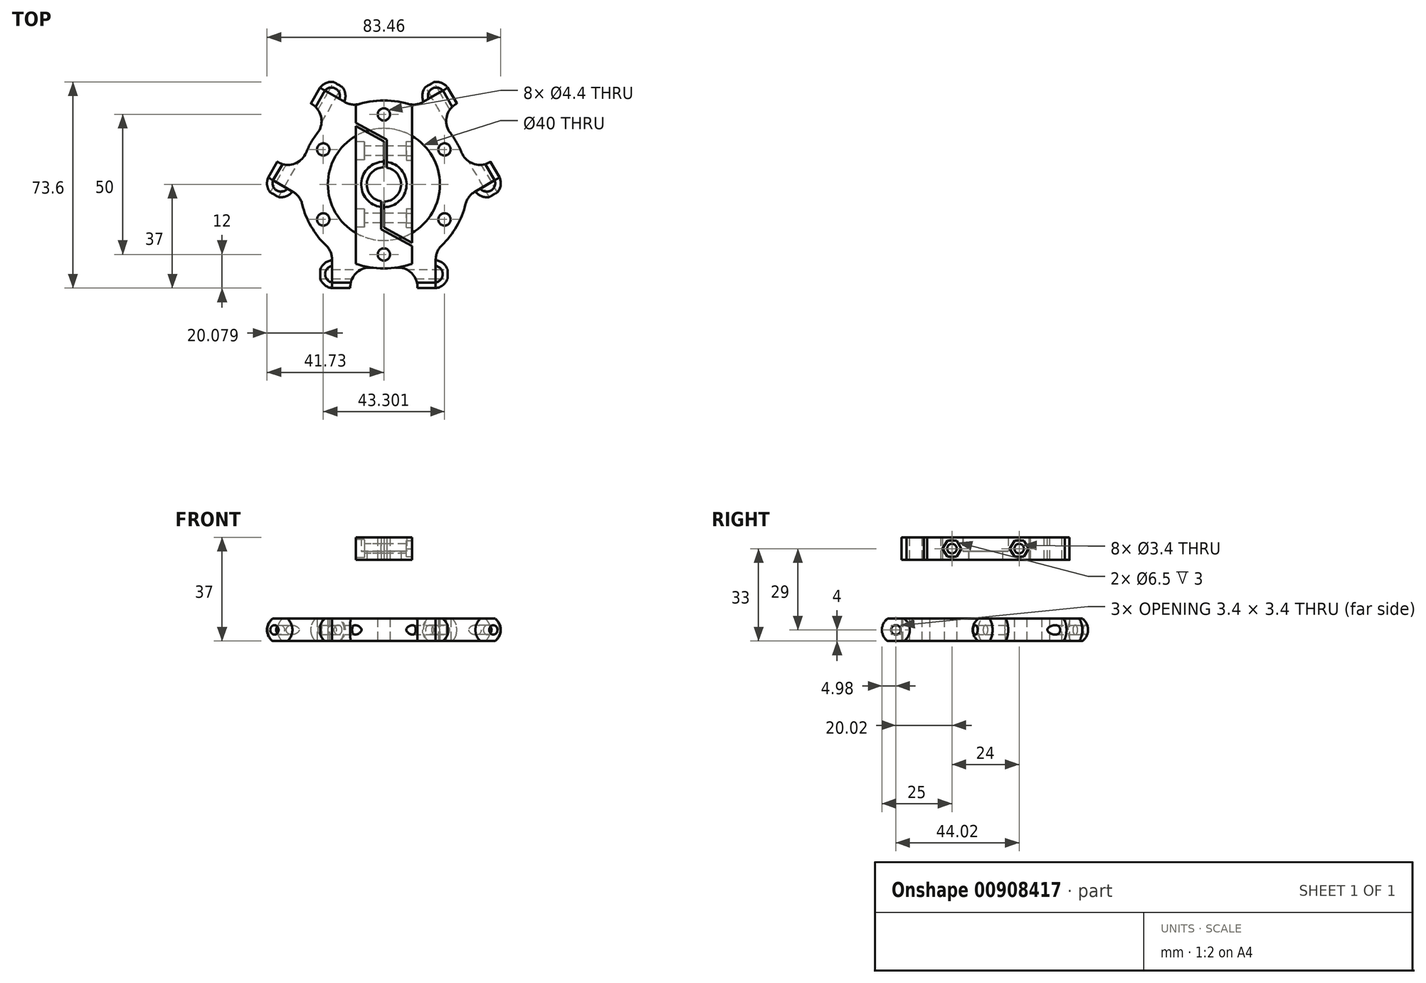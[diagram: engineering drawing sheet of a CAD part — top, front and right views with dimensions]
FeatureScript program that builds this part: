
annotation { "Feature Type Name" : "Feature", "Feature Type Description" : "" }
export const myFeature = defineFeature(function(context is Context, id is Id, definition is map)
    precondition{}
    {
        {
            var Q0;
            Q0=qCreatedBy(makeId("Top.planeOp"),FACE);
            var sketch = newSketch(context, id + "F0", { "sketchPlane" : qUnion([Q0])});
            skLineSegment(sketch, "E0", {"start": v(-16.34, 35.93) * mm, "end": v(-39.06, -3.47) * mm, "construction": true});
            skLineSegment(sketch, "E1", {"start": v(-40.4, -2.74) * mm, "end": v(-37.72, -4.2) * mm, "construction": true});
            skLineSegment(sketch, "E2", {"start": v(-17.63, 36.7) * mm, "end": v(-15.06, 35.15) * mm, "construction": true});
            skCircle(sketch, "E3", {"center": v(0, 0) * mm, "radius": 30 * mm});
            skCircle(sketch, "E4", {"center": v(0, 0) * mm, "radius": 20 * mm});
            skLineSegment(sketch, "E5", {"start": v(0, 0) * mm, "end": v(0, -43.55) * mm, "construction": true});
            skLineSegment(sketch, "E6", {"start": v(-25.45, -32) * mm, "end": v(35.74, -32) * mm, "construction": true});
            skLineSegment(sketch, "E7", {"start": v(-12, -37) * mm, "end": v(-12, -27.5) * mm});
            skLineSegment(sketch, "E8", {"start": v(-12, -37) * mm, "end": v(-18.5, -37) * mm});
            skLineSegment(sketch, "E9", {"start": v(-18.5, -37) * mm, "end": v(-18.5, -23.62) * mm});
            skLineSegment(sketch, "E10.MirrorCS", {"start": v(18.5, -37) * mm, "end": v(18.5, -23.62) * mm});
            skLineSegment(sketch, "E11.MirrorCS", {"start": v(12, -37) * mm, "end": v(12, -27.5) * mm});
            skLineSegment(sketch, "E12.MirrorCS", {"start": v(12, -37) * mm, "end": v(18.5, -37) * mm});
            skLineSegment(sketch, "E13.1.0", {"start": v(41.29, 2.48) * mm, "end": v(29.7, -4.21) * mm});
            skLineSegment(sketch, "E13.1.1", {"start": v(38.04, 8.1) * mm, "end": v(41.29, 2.48) * mm});
            skLineSegment(sketch, "E13.1.2", {"start": v(38.04, 8.1) * mm, "end": v(29.81, 3.36) * mm});
            skLineSegment(sketch, "E13.1.3", {"start": v(26.04, 28.9) * mm, "end": v(17.81, 24.14) * mm});
            skLineSegment(sketch, "E13.1.4", {"start": v(26.04, 28.9) * mm, "end": v(22.79, 34.52) * mm});
            skLineSegment(sketch, "E13.1.5", {"start": v(22.79, 34.52) * mm, "end": v(11.2, 27.83) * mm});
            skLineSegment(sketch, "E13.2.0", {"start": v(-22.79, 34.52) * mm, "end": v(-11.2, 27.83) * mm});
            skLineSegment(sketch, "E13.2.1", {"start": v(-26.04, 28.9) * mm, "end": v(-22.79, 34.52) * mm});
            skLineSegment(sketch, "E13.2.2", {"start": v(-26.04, 28.9) * mm, "end": v(-17.81, 24.14) * mm});
            skLineSegment(sketch, "E13.2.3", {"start": v(-38.04, 8.1) * mm, "end": v(-29.81, 3.36) * mm});
            skLineSegment(sketch, "E13.2.4", {"start": v(-38.04, 8.1) * mm, "end": v(-41.29, 2.48) * mm});
            skLineSegment(sketch, "E13.2.5", {"start": v(-41.29, 2.48) * mm, "end": v(-29.7, -4.21) * mm});
            skCircle(sketch, "E14", {"center": v(0, 25) * mm, "radius": 2.2 * mm});
            skCircle(sketch, "E15.1.0", {"center": v(-21.65, 12.5) * mm, "radius": 2.2 * mm});
            skCircle(sketch, "E15.2.0", {"center": v(-21.65, -12.5) * mm, "radius": 2.2 * mm});
            skCircle(sketch, "E15.3.0", {"center": v(0, -25) * mm, "radius": 2.2 * mm});
            skCircle(sketch, "E15.4.0", {"center": v(21.65, -12.5) * mm, "radius": 2.2 * mm});
            skCircle(sketch, "E15.5.0", {"center": v(21.65, 12.5) * mm, "radius": 2.2 * mm});
            skSolve(sketch);
        }
        {
            var Q0;
            Q0=qSketchRegion(id+"F0",true);
            extrude(context, id + "F1", {"entities" : qUnion([Q0]), "endBound" : BoundingType.SYMMETRIC, "depth" : 10 * mm, "offsetDistance" : 25 * mm});
        }
        {
            var Q0;
            Q0=qCreatedBy(makeId("Top.planeOp"),FACE);
            var sketch = newSketch(context, id + "F2", { "sketchPlane" : qUnion([Q0])});
            skArc(sketch, "E16", {"start": v(-23, -32.02) * mm, "mid": v(-21.7, -35.37) * mm, "end": v(-18.5, -37) * mm});
            skLineSegment(sketch, "E17", {"start": v(-18, -32.02) * mm, "end": v(-25.15, -32.02) * mm, "construction": true});
            skLineSegment(sketch, "E18", {"start": v(0, 0) * mm, "end": v(0, -44.37) * mm, "construction": true});
            skLineSegment(sketch, "E19", {"start": v(-39.92, 23.05) * mm, "end": v(0, 0) * mm, "construction": true});
            skLineSegment(sketch, "E20", {"start": v(0, 0) * mm, "end": v(41.5, 23.96) * mm, "construction": true});
            skLineSegment(sketch, "E21", {"start": v(-18.5, -37) * mm, "end": v(-18.5, -27.05) * mm});
            skLineSegment(sketch, "E22", {"start": v(-23, -32.02) * mm, "end": v(-18.5, -32.02) * mm});
            skArc(sketch, "E23.1.0", {"start": v(39.23, -3.9) * mm, "mid": v(41.49, -1.11) * mm, "end": v(41.29, 2.48) * mm});
            skLineSegment(sketch, "E23.1.1", {"start": v(39.23, -3.9) * mm, "end": v(36.98, -0.01) * mm});
            skArc(sketch, "E23.2.0", {"start": v(-16.23, 35.93) * mm, "mid": v(-19.78, 36.49) * mm, "end": v(-22.79, 34.52) * mm});
            skLineSegment(sketch, "E23.2.1", {"start": v(-16.23, 35.93) * mm, "end": v(-18.48, 32.03) * mm});
            skPoint(sketch, "E23.center", {"position": v(0, 0) * mm});
            skLineSegment(sketch, "E24.MirrorCS", {"start": v(23, -32.02) * mm, "end": v(18.5, -32.02) * mm});
            skLineSegment(sketch, "E25.MirrorCS", {"start": v(18, -32.02) * mm, "end": v(25.15, -32.02) * mm, "construction": true});
            skLineSegment(sketch, "E26.MirrorCS", {"start": v(18.5, -37) * mm, "end": v(18.5, -27.05) * mm});
            skArc(sketch, "E27.MirrorCS", {"start": v(23, -32.02) * mm, "mid": v(21.7, -35.37) * mm, "end": v(18.5, -37) * mm});
            skSolve(sketch);
        }
        {
            var Q0;
            Q0=qSketchRegion(id+"F2",true);
            var Q1;
            Q1=sQuery(id+"F2.wireOp",EDGE,"E17");
            revolve(context, id + "F3", {"surfaceOperationType" : NewSurfaceOperationType.NEW, "entities" : qUnion([Q0]), "axis" : qUnion([Q1]), "revolveType" : RevolveType.FULL});
        }
        {
            var Q0;
            Q0=qCreatedBy(makeId("Right.planeOp"),FACE);
            var sketch = newSketch(context, id + "F4", { "sketchPlane" : qUnion([Q0])});
            skLineSegment(sketch, "E28", {"start": v(0, 32.68) * mm, "end": v(0, -16.38) * mm, "construction": true});
            skSolve(sketch);
        }
        {
            var Q0;
            Q0=makeQuery(id+"F3.opRevolve","SWEPT_BODY",BODY,{"disambiguationData":[OSD([sQuery(id+"F2.wireOp",EDGE,"E16"),sQuery(id+"F2.wireOp",EDGE,"E21"),sQuery(id+"F2.wireOp",EDGE,"E22")])]});
            var Q1;
            Q1=makeQuery(id+"F3.opRevolve","SWEPT_BODY",BODY,{"disambiguationData":[OSD([sQuery(id+"F2.wireOp",EDGE,"E24.MirrorCS"),sQuery(id+"F2.wireOp",EDGE,"E26.MirrorCS"),sQuery(id+"F2.wireOp",EDGE,"E27.MirrorCS")])]});
            var Q2;
            Q2=sQuery(id+"F4.wireOp",EDGE,"E28");
            circularPattern(context, id + "F5", {"entities" : qUnion([Q0, Q1]), "axis" : qUnion([Q2]), "angle" : 360 * degree, "instanceCount" : 3, "equalSpace" : true});
        }
        {
            var Q0;
            Q0=makeQuery(id+"F1.opExtrude","CAP_EDGE",EDGE,{"disambiguationData":[OSD([sQuery(id+"F0.wireOp",EDGE,"E13.2.1")])],"isStart":false});
            var Q1;
            Q1=makeQuery(id+"F1.opExtrude","CAP_EDGE",EDGE,{"disambiguationData":[OSD([sQuery(id+"F0.wireOp",EDGE,"E13.2.4")])],"isStart":false});
            var Q2;
            Q2=makeQuery(id+"F1.opExtrude","CAP_EDGE",EDGE,{"disambiguationData":[OSD([sQuery(id+"F0.wireOp",EDGE,"E13.1.4")])],"isStart":false});
            var Q3;
            Q3=makeQuery(id+"F1.opExtrude","CAP_EDGE",EDGE,{"disambiguationData":[OSD([sQuery(id+"F0.wireOp",EDGE,"E13.1.1")])],"isStart":false});
            var Q4;
            Q4=makeQuery(id+"F1.opExtrude","CAP_EDGE",EDGE,{"disambiguationData":[OSD([sQuery(id+"F0.wireOp",EDGE,"E12.MirrorCS")])],"isStart":false});
            var Q5;
            Q5=makeQuery(id+"F1.opExtrude","CAP_EDGE",EDGE,{"disambiguationData":[OSD([sQuery(id+"F0.wireOp",EDGE,"E8")])],"isStart":false});
            var Q6;
            Q6=makeQuery(id+"F1.opExtrude","CAP_EDGE",EDGE,{"disambiguationData":[OSD([sQuery(id+"F0.wireOp",EDGE,"E8")])],"isStart":true});
            var Q7;
            Q7=makeQuery(id+"F1.opExtrude","CAP_EDGE",EDGE,{"disambiguationData":[OSD([sQuery(id+"F0.wireOp",EDGE,"E12.MirrorCS")])],"isStart":true});
            var Q8;
            Q8=makeQuery(id+"F1.opExtrude","CAP_EDGE",EDGE,{"disambiguationData":[OSD([sQuery(id+"F0.wireOp",EDGE,"E13.1.1")])],"isStart":true});
            var Q9;
            Q9=makeQuery(id+"F1.opExtrude","CAP_EDGE",EDGE,{"disambiguationData":[OSD([sQuery(id+"F0.wireOp",EDGE,"E13.1.4")])],"isStart":true});
            var Q10;
            Q10=makeQuery(id+"F1.opExtrude","CAP_EDGE",EDGE,{"disambiguationData":[OSD([sQuery(id+"F0.wireOp",EDGE,"E13.2.1")])],"isStart":true});
            var Q11;
            Q11=makeQuery(id+"F1.opExtrude","CAP_EDGE",EDGE,{"disambiguationData":[OSD([sQuery(id+"F0.wireOp",EDGE,"E13.2.4")])],"isStart":true});
            fillet(context, id + "F6", {"entities" : qUnion([Q0, Q1, Q2, Q3, Q4, Q5, Q6, Q7, Q8, Q9, Q10, Q11]), "radius" : 5 * mm, "tangentPropagation" : true, "allowEdgeOverflow" : false});
        }
        {
            var Q0;
            Q0=qCreatedBy(makeId("Top.planeOp"),FACE);
            var sketch = newSketch(context, id + "F7", { "sketchPlane" : qUnion([Q0])});
            skCircle(sketch, "E29", {"center": v(0, 0) * mm, "radius": 54.32 * mm});
            skSolve(sketch);
        }
        {
            var Q0;
            Q0=makeQuery(id+"F7.imprint","IMPRINT",FACE,{"disambiguationData":[TD([[makeQuery(id+"F7.imprint","IMPRINT",EDGE,{"derivedFrom":sQuery(id+"F7.wireOp",EDGE,"E29")}),1.0]])]});
            extrude(context, id + "F8", {"entities" : qUnion([Q0]), "operationType" : NewBodyOperationType.REMOVE, "depth" : 10 * mm, "offsetDistance" : 25 * mm, "hasSecondDirection" : true, "secondDirectionOppositeDirection" : false, "secondDirectionDepth" : 4 * mm});
        }
        {
            var Q0;
            Q0=makeQuery(id+"F7.imprint","IMPRINT",FACE,{"disambiguationData":[TD([[makeQuery(id+"F7.imprint","IMPRINT",EDGE,{"derivedFrom":sQuery(id+"F7.wireOp",EDGE,"E29")}),1.0]])]});
            extrude(context, id + "F9", {"entities" : qUnion([Q0]), "operationType" : NewBodyOperationType.REMOVE, "oppositeDirection" : true, "depth" : 20 * mm, "offsetDistance" : 25 * mm, "hasSecondDirection" : true, "secondDirectionOppositeDirection" : true, "secondDirectionDepth" : 4 * mm});
        }
        {
            var Q0;
            Q0=qCreatedBy(makeId("Right.planeOp"),FACE);
            var sketch = newSketch(context, id + "F10", { "sketchPlane" : qUnion([Q0])});
            skCircle(sketch, "E30", {"center": v(-32.02, 0) * mm, "radius": 1.7 * mm});
            skSolve(sketch);
        }
        {
            var Q0;
            Q0=qSketchRegion(id+"F10",true);
            extrude(context, id + "F11", {"entities" : qUnion([Q0]), "operationType" : NewBodyOperationType.REMOVE, "endBound" : BoundingType.SYMMETRIC, "oppositeDirection" : true, "depth" : 80 * mm, "offsetDistance" : 25 * mm});
        }
        {
            var Q0;
            Q0=sQuery(id+"F2.wireOp",EDGE,"E19");
            cPlane(context, id + "F12", {"entities" : qUnion([Q0]), "cplaneType" : CPlaneType.LINE_ANGLE, "offset" : 25 * mm, "angle" : 0 * degree, "width" : 150 * mm, "height" : 150 * mm});
        }
        {
            var Q0;
            Q0=qCreatedBy(id+"F12.planeOp",FACE);
            var sketch = newSketch(context, id + "F13", { "sketchPlane" : qUnion([Q0])});
            skCircle(sketch, "E31", {"center": v(32.02, 0) * mm, "radius": 1.7 * mm});
            skSolve(sketch);
        }
        {
            var Q0;
            Q0=qSketchRegion(id+"F13",true);
            extrude(context, id + "F14", {"entities" : qUnion([Q0]), "operationType" : NewBodyOperationType.REMOVE, "endBound" : BoundingType.SYMMETRIC, "oppositeDirection" : true, "depth" : 80 * mm, "offsetDistance" : 25 * mm});
        }
        {
            var Q0;
            Q0=sQuery(id+"F2.wireOp",EDGE,"E20");
            cPlane(context, id + "F15", {"entities" : qUnion([Q0]), "cplaneType" : CPlaneType.LINE_ANGLE, "offset" : 25 * mm, "angle" : 0 * degree, "width" : 150 * mm, "height" : 150 * mm});
        }
        {
            var Q0;
            Q0=qCreatedBy(id+"F15.planeOp",FACE);
            var sketch = newSketch(context, id + "F16", { "sketchPlane" : qUnion([Q0])});
            skCircle(sketch, "E32", {"center": v(-32.02, 0) * mm, "radius": 1.7 * mm});
            skSolve(sketch);
        }
        {
            var Q0;
            Q0=qSketchRegion(id+"F16",true);
            extrude(context, id + "F17", {"entities" : qUnion([Q0]), "operationType" : NewBodyOperationType.REMOVE, "endBound" : BoundingType.SYMMETRIC, "oppositeDirection" : true, "depth" : 80 * mm, "offsetDistance" : 25 * mm});
        }
        {
            var Q0;
            Q0=makeQuery(id+"F1.opExtrude","SWEPT_EDGE",EDGE,{"disambiguationData":[OSD([sQuery(id+"F0.wireOp",EDGE,"E3"),sQuery(id+"F0.wireOp",EDGE,"E13.2.0")])]});
            var Q1;
            Q1=makeQuery(id+"F1.opExtrude","SWEPT_EDGE",EDGE,{"disambiguationData":[OSD([sQuery(id+"F0.wireOp",EDGE,"E3"),sQuery(id+"F0.wireOp",EDGE,"E13.1.5")])]});
            var Q2;
            Q2=makeQuery(id+"F1.opExtrude","SWEPT_EDGE",EDGE,{"disambiguationData":[OSD([sQuery(id+"F0.wireOp",EDGE,"E3"),sQuery(id+"F0.wireOp",EDGE,"E13.1.0")])]});
            var Q3;
            Q3=makeQuery(id+"F1.opExtrude","SWEPT_EDGE",EDGE,{"disambiguationData":[OSD([sQuery(id+"F0.wireOp",EDGE,"E3"),sQuery(id+"F0.wireOp",EDGE,"E10.MirrorCS")])]});
            var Q4;
            Q4=makeQuery(id+"F1.opExtrude","SWEPT_EDGE",EDGE,{"disambiguationData":[OSD([sQuery(id+"F0.wireOp",EDGE,"E3"),sQuery(id+"F0.wireOp",EDGE,"E13.2.5")])]});
            var Q5;
            Q5=makeQuery(id+"F1.opExtrude","SWEPT_EDGE",EDGE,{"disambiguationData":[OSD([sQuery(id+"F0.wireOp",EDGE,"E3"),sQuery(id+"F0.wireOp",EDGE,"E9")])]});
            fillet(context, id + "F18", {"entities" : qUnion([Q0, Q1, Q2, Q3, Q4, Q5]), "radius" : 7 * mm, "tangentPropagation" : true, "allowEdgeOverflow" : false});
        }
        {
            var Q0;
            Q0=qCreatedBy(makeId("Top.planeOp"),FACE);
            cPlane(context, id + "F19", {"entities" : qUnion([Q0]), "cplaneType" : CPlaneType.OFFSET, "offset" : 25 * mm, "width" : 150 * mm, "height" : 150 * mm});
        }
        {
            var Q0;
            Q0=qCreatedBy(id+"F19.planeOp",FACE);
            var sketch = newSketch(context, id + "F20", { "sketchPlane" : qUnion([Q0])});
            skCircle(sketch, "E33", {"center": v(0, 25) * mm, "radius": 2.2 * mm});
            skCircle(sketch, "E34", {"center": v(0, -25) * mm, "radius": 2.2 * mm});
            skArc(sketch, "E35", {"start": v(10, 28.28) * mm, "mid": v(0, 30) * mm, "end": v(-10, 28.28) * mm});
            skLineSegment(sketch, "E36", {"start": v(-10, 28.28) * mm, "end": v(-10, -28.28) * mm});
            skLineSegment(sketch, "E37", {"start": v(10, -28.28) * mm, "end": v(10, 28.28) * mm});
            skArc(sketch, "E38.trimOffspring", {"start": v(-10, -28.28) * mm, "mid": v(0, -30) * mm, "end": v(10, -28.28) * mm});
            skSolve(sketch);
        }
        {
            var Q0;
            Q0=makeQuery(id+"F20.imprint","IMPRINT",FACE,{"disambiguationData":[TD([[makeQuery(id+"F20.imprint","IMPRINT",EDGE,{"derivedFrom":sQuery(id+"F20.wireOp",EDGE,"E33")}),-1.0]])]});
            extrude(context, id + "F21", {"entities" : qUnion([Q0]), "depth" : 8 * mm, "offsetDistance" : 25 * mm});
        }
        {
            var Q0;
            Q0=makeQuery(id+"F21.opExtrude","CAP_FACE",FACE,{"disambiguationData":[OSD([sQuery(id+"F20.wireOp",EDGE,"E33"),sQuery(id+"F20.wireOp",EDGE,"E34"),sQuery(id+"F20.wireOp",EDGE,"E35"),sQuery(id+"F20.wireOp",EDGE,"E36"),sQuery(id+"F20.wireOp",EDGE,"E37"),sQuery(id+"F20.wireOp",EDGE,"E38.trimOffspring")])],"isStart":true});
            var sketch = newSketch(context, id + "F22", { "sketchPlane" : qUnion([Q0])});
            skCircle(sketch, "E39", {"center": v(0, 0) * mm, "radius": 6.1 * mm});
            skCircle(sketch, "E40", {"center": v(0, 0) * mm, "radius": 8.1 * mm});
            skLineSegment(sketch, "E41", {"start": v(-10, -20.86) * mm, "end": v(0, -15.4) * mm});
            skLineSegment(sketch, "E42", {"start": v(1, 0) * mm, "end": v(1, -16) * mm});
            skLineSegment(sketch, "E43", {"start": v(1, -16) * mm, "end": v(-10, -22) * mm});
            skLineSegment(sketch, "E44", {"start": v(-10, -22) * mm, "end": v(10, -22) * mm, "construction": true});
            skLineSegment(sketch, "E45", {"start": v(-10, -22) * mm, "end": v(-10, -20.86) * mm});
            skLineSegment(sketch, "E46", {"start": v(0, -15.4) * mm, "end": v(0, 0) * mm});
            skLineSegment(sketch, "E47", {"start": v(0, 0) * mm, "end": v(1, 0) * mm});
            skLineSegment(sketch, "E48.1.0", {"start": v(10, 22) * mm, "end": v(10, 20.86) * mm});
            skLineSegment(sketch, "E48.1.1", {"start": v(10, 20.86) * mm, "end": v(0, 15.4) * mm});
            skLineSegment(sketch, "E48.1.2", {"start": v(-1, 16) * mm, "end": v(10, 22) * mm});
            skLineSegment(sketch, "E48.1.3", {"start": v(0, 15.4) * mm, "end": v(0, 0) * mm});
            skLineSegment(sketch, "E48.1.4", {"start": v(-1, 0) * mm, "end": v(-1, 16) * mm});
            skLineSegment(sketch, "E48.1.5", {"start": v(0, 0) * mm, "end": v(-1, 0) * mm});
            skSolve(sketch);
        }
        {
            var Q0;
            Q0=makeQuery(id+"F22.imprint","IMPRINT",FACE,{"disambiguationData":[TD([[makeQuery(id+"F22.imprint","IMPRINT",EDGE,{"derivedFrom":sQuery(id+"F22.wireOp",EDGE,"E39")}),1.0]])]});
            var Q1;
            Q1=makeQuery(id+"F21.opExtrude","CAP_FACE",FACE,{"disambiguationData":[OSD([sQuery(id+"F20.wireOp",EDGE,"E33"),sQuery(id+"F20.wireOp",EDGE,"E34"),sQuery(id+"F20.wireOp",EDGE,"E35"),sQuery(id+"F20.wireOp",EDGE,"E36"),sQuery(id+"F20.wireOp",EDGE,"E37"),sQuery(id+"F20.wireOp",EDGE,"E38.trimOffspring")])],"isStart":false});
            extrude(context, id + "F23", {"entities" : qUnion([Q0]), "operationType" : NewBodyOperationType.REMOVE, "endBound" : BoundingType.UP_TO_SURFACE, "oppositeDirection" : true, "depth" : 25 * mm, "endBoundEntityFace" : qUnion([Q1]), "offsetDistance" : 25 * mm});
        }
        {
            var Q0;
            Q0=makeQuery(id+"F22.imprint","IMPRINT",FACE,{"disambiguationData":[TD([[makeQuery(id+"F22.imprint","IMPRINT",EDGE,{"derivedFrom":sQuery(id+"F22.wireOp",EDGE,"E48.1.0")}),-1.0]])]});
            var Q1;
            {var subQ0=sQuery(id+"F22.wireOp",EDGE,"E48.1.4");var subQ1=sQuery(id+"F22.wireOp",EDGE,"E39");var subQ2=makeQuery(id+"F22.imprint","INTERSECT",VERTEX,{"derivedFrom":[subQ1,subQ0]});Q1=makeQuery(id+"F22.imprint","IMPRINT",FACE,{"disambiguationData":[TD([[makeQuery(id+"F22.imprint","IMPRINT",EDGE,{"disambiguationData":[TD([[subQ2,1.0]])],"derivedFrom":subQ1}),-1.0]])]});}
            var Q2;
            {var subQ1=sQuery(id+"F22.wireOp",EDGE,"E41");Q2=makeQuery(id+"F22.imprint","IMPRINT",FACE,{"disambiguationData":[TD([[makeQuery(id+"F22.imprint","IMPRINT",EDGE,{"derivedFrom":subQ1}),-1.0]])]});}
            var Q3;
            {var subQ0=sQuery(id+"F22.wireOp",EDGE,"E46");var subQ1=sQuery(id+"F22.wireOp",EDGE,"E39");var subQ2=makeQuery(id+"F22.imprint","INTERSECT",VERTEX,{"derivedFrom":[subQ1,subQ0]});Q3=makeQuery(id+"F22.imprint","IMPRINT",FACE,{"disambiguationData":[TD([[makeQuery(id+"F22.imprint","IMPRINT",EDGE,{"disambiguationData":[TD([[subQ2,-1.0]])],"derivedFrom":subQ1}),-1.0]])]});}
            var Q4;
            Q4=makeQuery(id+"F21.opExtrude","CAP_FACE",FACE,{"disambiguationData":[OSD([sQuery(id+"F20.wireOp",EDGE,"E33"),sQuery(id+"F20.wireOp",EDGE,"E34"),sQuery(id+"F20.wireOp",EDGE,"E35"),sQuery(id+"F20.wireOp",EDGE,"E36"),sQuery(id+"F20.wireOp",EDGE,"E37"),sQuery(id+"F20.wireOp",EDGE,"E38.trimOffspring")])],"isStart":false});
            extrude(context, id + "F24", {"entities" : qUnion([Q0, Q1, Q2, Q3]), "operationType" : NewBodyOperationType.REMOVE, "endBound" : BoundingType.UP_TO_SURFACE, "oppositeDirection" : true, "depth" : 25 * mm, "endBoundEntityFace" : qUnion([Q4]), "offsetDistance" : 25 * mm});
        }
        {
            var Q0;
            {var subQ3=sQuery(id+"F22.wireOp",EDGE,"00b420b3-74bb-4662-af47-3d81f60943aa.1.3");var subQ5=sQuery(id+"F22.wireOp",EDGE,"E40");var subQ6=makeQuery(id+"F22.imprint","INTERSECT",VERTEX,{"derivedFrom":[subQ5,subQ3]});Q0=makeQuery(id+"F22.imprint","IMPRINT",FACE,{"disambiguationData":[TD([[makeQuery(id+"F22.imprint","IMPRINT",EDGE,{"disambiguationData":[TD([[subQ6,-1.0]])],"derivedFrom":subQ5}),1.0]])]});}
            var Q1;
            {var subQ3=sQuery(id+"F22.wireOp",EDGE,"00b420b3-74bb-4662-af47-3d81f60943aa.1.2");var subQ5=sQuery(id+"F22.wireOp",EDGE,"E40");var subQ6=makeQuery(id+"F22.imprint","INTERSECT",VERTEX,{"derivedFrom":[subQ5,subQ3]});Q1=makeQuery(id+"F22.imprint","IMPRINT",FACE,{"disambiguationData":[TD([[makeQuery(id+"F22.imprint","IMPRINT",EDGE,{"disambiguationData":[TD([[subQ6,1.0]])],"derivedFrom":subQ5}),1.0]])]});}
            extrude(context, id + "F25", {"entities" : qUnion([Q0, Q1]), "operationType" : NewBodyOperationType.REMOVE, "oppositeDirection" : true, "depth" : 20 * mm, "offsetDistance" : 25 * mm, "hasSecondDirection" : true, "secondDirectionOppositeDirection" : true, "secondDirectionDepth" : 3 * mm});
        }
        {
            var Q0;
            {var subQ0=sQuery(id+"F20.wireOp",EDGE,"E38.trimOffspring");var subQ2=sQuery(id+"F20.wireOp",EDGE,"E36");Q0=makeQuery(id+"F24.boolean.opBoolean","SPLIT",FACE,{"disambiguationData":[TD([makeQuery(id+"F21.opExtrude","SWEPT_FACE",FACE,{"disambiguationData":[OSD([subQ0])]})])],"derivedFrom":makeQuery(id+"F21.opExtrude","SWEPT_FACE",FACE,{"disambiguationData":[OSD([subQ2])]})});}
            var sketch = newSketch(context, id + "F26", { "sketchPlane" : qUnion([Q0])});
            skPoint(sketch, "E49", {"position": v(-12, 29) * mm});
            skPoint(sketch, "E49.positionSnap0", {"position": v(-20.86, 29) * mm});
            skPoint(sketch, "E50", {"position": v(12, 29) * mm});
            skSolve(sketch);
        }
        {
            var Q0;
            Q0=sQuery(id+"F26.wireOp",VERTEX,"E49");
            var Q1;
            Q1=sQuery(id+"F26.wireOp",VERTEX,"E50");
            var Q2;
            Q2=makeQuery(id+"F24.boolean.opBoolean","SPLIT",BODY,{"disambiguationData":[OD(0.0)],"derivedFrom":makeQuery(id+"F21.opExtrude","SWEPT_BODY",BODY,{"disambiguationData":[OSD([sQuery(id+"F20.wireOp",EDGE,"E33"),sQuery(id+"F20.wireOp",EDGE,"E34"),sQuery(id+"F20.wireOp",EDGE,"E35"),sQuery(id+"F20.wireOp",EDGE,"E36"),sQuery(id+"F20.wireOp",EDGE,"E37"),sQuery(id+"F20.wireOp",EDGE,"E38.trimOffspring")])]})});
            var Q3;
            Q3=makeQuery(id+"F24.boolean.opBoolean","SPLIT",BODY,{"disambiguationData":[OD(1.0)],"derivedFrom":makeQuery(id+"F21.opExtrude","SWEPT_BODY",BODY,{"disambiguationData":[OSD([sQuery(id+"F20.wireOp",EDGE,"E33"),sQuery(id+"F20.wireOp",EDGE,"E34"),sQuery(id+"F20.wireOp",EDGE,"E35"),sQuery(id+"F20.wireOp",EDGE,"E36"),sQuery(id+"F20.wireOp",EDGE,"E37"),sQuery(id+"F20.wireOp",EDGE,"E38.trimOffspring")])]})});
            hole(context, id + "F27", {"style" : HoleStyle.C_BORE, "endStyle" : HoleEndStyle.THROUGH, "standardTappedOrClearance" : lookupTablePath({ "fit" : "Normal", "standard" : "ISO", "size" : "M3", "type" : "Clearance" }), "standardBlindInLast" : lookupTablePath({ "fit" : "Normal", "standard" : "ISO", "size" : "M3", "type" : "Clearance" }), "holeDiameter" : 3.4 * mm, "cBoreDiameter" : 6.5 * mm, "cBoreDepth" : 3 * mm, "majorDiameter" : 5 * mm, "isTappedThrough" : true, "tappedDepth" : 12 * mm, "tapClearance" : 3, "locations" : qUnion([Q0, Q1]), "scope" : qUnion([Q2, Q3])});
        }
        {
            var Q0;
            {var subQ1=sQuery(id+"F20.wireOp",EDGE,"E37");var subQ3=sQuery(id+"F20.wireOp",EDGE,"E35");Q0=makeQuery(id+"F24.boolean.opBoolean","SPLIT",FACE,{"disambiguationData":[TD([makeQuery(id+"F21.opExtrude","SWEPT_FACE",FACE,{"disambiguationData":[OSD([subQ3])]})])],"derivedFrom":makeQuery(id+"F21.opExtrude","SWEPT_FACE",FACE,{"disambiguationData":[OSD([subQ1])]})});}
            var sketch = newSketch(context, id + "F28", { "sketchPlane" : qUnion([Q0])});
            skCircle(sketch, "E51.cCircle", {"center": v(-12, 29) * mm, "radius": 2.9 * mm, "construction": true});
            skLineSegment(sketch, "E51.0", {"start": v(-10.33, 26.1) * mm, "end": v(-13.67, 26.1) * mm});
            skLineSegment(sketch, "E51.1", {"start": v(-13.67, 26.1) * mm, "end": v(-15.35, 29) * mm});
            skLineSegment(sketch, "E51.2", {"start": v(-15.35, 29) * mm, "end": v(-13.67, 31.9) * mm});
            skLineSegment(sketch, "E51.3", {"start": v(-13.67, 31.9) * mm, "end": v(-10.33, 31.9) * mm});
            skLineSegment(sketch, "E51.4", {"start": v(-10.33, 31.9) * mm, "end": v(-8.65, 29) * mm});
            skLineSegment(sketch, "E51.5", {"start": v(-8.65, 29) * mm, "end": v(-10.33, 26.1) * mm});
            skPoint(sketch, "E51.0.midPoint", {"position": v(-12, 26.1) * mm});
            skLineSegment(sketch, "E52.MirrorCS", {"start": v(10.33, 26.1) * mm, "end": v(13.67, 26.1) * mm});
            skLineSegment(sketch, "E53.MirrorCS", {"start": v(13.67, 31.9) * mm, "end": v(10.33, 31.9) * mm});
            skLineSegment(sketch, "E54.MirrorCS", {"start": v(13.67, 26.1) * mm, "end": v(15.35, 29) * mm});
            skLineSegment(sketch, "E55.MirrorCS", {"start": v(10.33, 31.9) * mm, "end": v(8.65, 29) * mm});
            skLineSegment(sketch, "E56.MirrorCS", {"start": v(15.35, 29) * mm, "end": v(13.67, 31.9) * mm});
            skCircle(sketch, "E57.MirrorC", {"center": v(12, 29) * mm, "radius": 2.9 * mm, "construction": true});
            skPoint(sketch, "E58.MirrorP", {"position": v(12, 26.1) * mm});
            skLineSegment(sketch, "E59.MirrorCS", {"start": v(8.65, 29) * mm, "end": v(10.33, 26.1) * mm});
            skSolve(sketch);
        }
        {
            var Q0;
            Q0=qSketchRegion(id+"F28",true);
            extrude(context, id + "F29", {"entities" : qUnion([Q0]), "operationType" : NewBodyOperationType.REMOVE, "oppositeDirection" : true, "depth" : 2 * mm, "offsetDistance" : 25 * mm});
        }
    });
